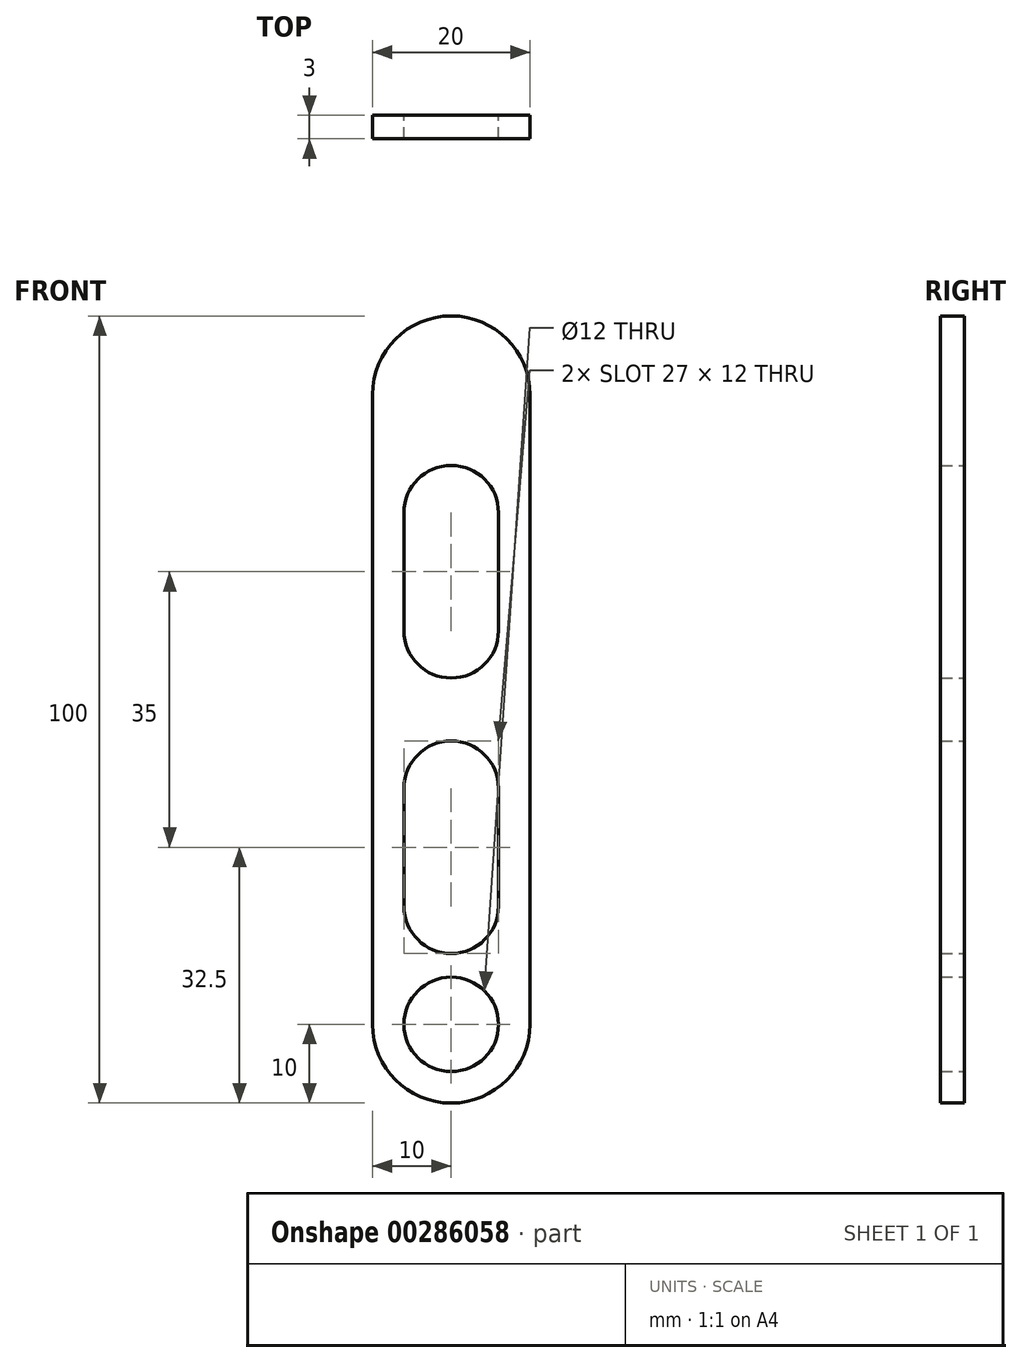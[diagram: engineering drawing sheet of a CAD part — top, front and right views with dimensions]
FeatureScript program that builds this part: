
annotation { "Feature Type Name" : "Feature", "Feature Type Description" : "" }
export const myFeature = defineFeature(function(context is Context, id is Id, definition is map)
    precondition{}
    {
        {
            var Q0;
            Q0=qCreatedBy(makeId("Front.planeOp"),FACE);
            var sketch = newSketch(context, id + "F0", { "sketchPlane" : qUnion([Q0])});
            skLineSegment(sketch, "E0.bottom", {"start": v(10, -40) * mm, "end": v(-10, -40) * mm, "construction": true});
            skLineSegment(sketch, "E0.top", {"start": v(10, 40) * mm, "end": v(-10, 40) * mm, "construction": true});
            skLineSegment(sketch, "E0.left", {"start": v(10, -40) * mm, "end": v(10, 40) * mm});
            skLineSegment(sketch, "E0.right", {"start": v(-10, -40) * mm, "end": v(-10, 40) * mm});
            skPoint(sketch, "E0.middle", {"position": v(0, 0) * mm});
            skArc(sketch, "E1", {"start": v(10, 40) * mm, "mid": v(0, 50) * mm, "end": v(-10, 40) * mm});
            skArc(sketch, "E2", {"start": v(-10, -40) * mm, "mid": v(0, -50) * mm, "end": v(10, -40) * mm});
            skCircle(sketch, "E3", {"center": v(0, -40) * mm, "radius": 6 * mm});
            skLineSegment(sketch, "E4", {"start": v(6, -40) * mm, "end": v(6, 40) * mm, "construction": true});
            skLineSegment(sketch, "E5", {"start": v(-6, -40) * mm, "end": v(-6, 40) * mm, "construction": true});
            skLineSegment(sketch, "E6", {"start": v(6, -25) * mm, "end": v(6, -10) * mm});
            skLineSegment(sketch, "E7", {"start": v(-6, -10) * mm, "end": v(-6, -25) * mm});
            skLineSegment(sketch, "E8", {"start": v(6, 10) * mm, "end": v(6, 25) * mm});
            skLineSegment(sketch, "E9", {"start": v(-6, 25) * mm, "end": v(-6, 10) * mm});
            skArc(sketch, "E10", {"start": v(-6, -25) * mm, "mid": v(0, -31) * mm, "end": v(6, -25) * mm});
            skArc(sketch, "E11", {"start": v(6, -10) * mm, "mid": v(0, -4) * mm, "end": v(-6, -10) * mm});
            skArc(sketch, "E12", {"start": v(-6, 10) * mm, "mid": v(0, 4) * mm, "end": v(6, 10) * mm});
            skArc(sketch, "E13", {"start": v(6, 25) * mm, "mid": v(0, 31) * mm, "end": v(-6, 25) * mm});
            skCircle(sketch, "E14", {"center": v(0, 40) * mm, "radius": 6 * mm, "construction": true});
            skSolve(sketch);
        }
        {
            var Q0;
            Q0=makeQuery(id+"F0.imprint","IMPRINT",FACE,{"disambiguationData":[TD([[makeQuery(id+"F0.imprint","IMPRINT",EDGE,{"derivedFrom":sQuery(id+"F0.wireOp",EDGE,"E0.left")}),1.0]])]});
            extrude(context, id + "F1", {"entities" : qUnion([Q0]), "depth" : 3 * mm});
        }
    });
